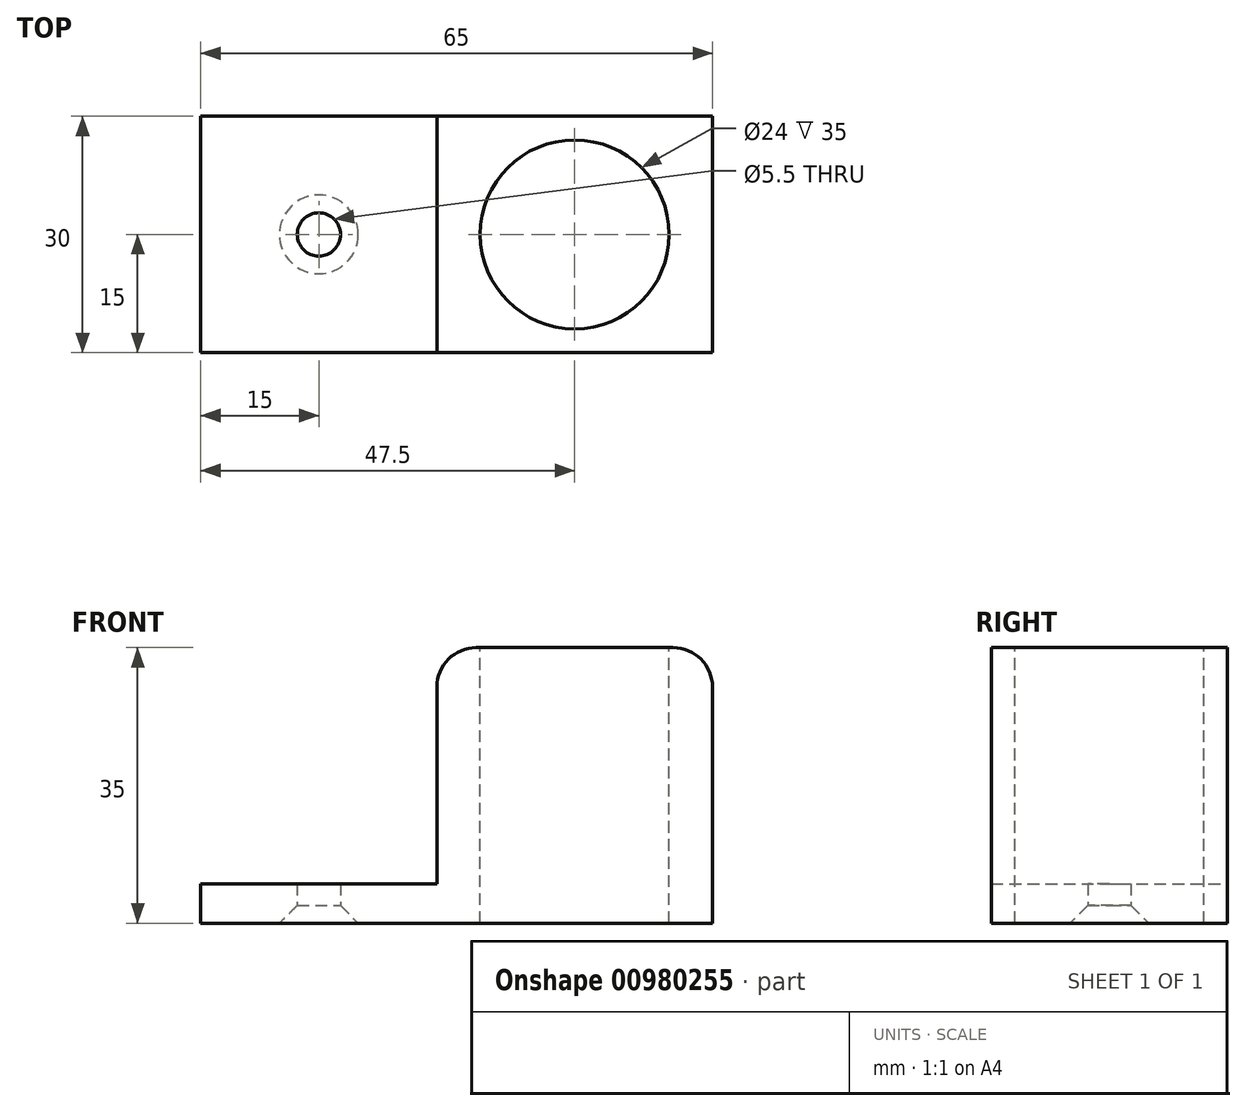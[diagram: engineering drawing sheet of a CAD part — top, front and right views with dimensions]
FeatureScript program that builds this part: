
annotation { "Feature Type Name" : "Feature", "Feature Type Description" : "" }
export const myFeature = defineFeature(function(context is Context, id is Id, definition is map)
    precondition{}
    {
        {
            var Q0;
            Q0=qCreatedBy(makeId("Front.planeOp"),FACE);
            var sketch = newSketch(context, id + "F0", { "sketchPlane" : qUnion([Q0])});
            skLineSegment(sketch, "E0", {"start": v(0, 0) * mm, "end": v(-65, 0) * mm});
            skLineSegment(sketch, "E1", {"start": v(-65, 0) * mm, "end": v(-65, 5) * mm});
            skLineSegment(sketch, "E2", {"start": v(-65, 5) * mm, "end": v(-35, 5) * mm});
            skLineSegment(sketch, "E3", {"start": v(-35, 5) * mm, "end": v(-35, 35) * mm});
            skLineSegment(sketch, "E4", {"start": v(-35, 35) * mm, "end": v(0, 35) * mm});
            skLineSegment(sketch, "E5", {"start": v(0, 35) * mm, "end": v(0, 0) * mm});
            skSolve(sketch);
        }
        {
            var Q0;
            Q0=makeQuery(id+"F0.imprint","IMPRINT",FACE,{"disambiguationData":[TD([[makeQuery(id+"F0.imprint","IMPRINT",EDGE,{"derivedFrom":sQuery(id+"F0.wireOp",EDGE,"E0")}),-1.0]])]});
            extrude(context, id + "F1", {"entities" : qUnion([Q0]), "depth" : 30 * mm, "offsetDistance" : 25 * mm});
        }
        {
            var Q0;
            Q0=makeQuery(id+"F1.opExtrude","SWEPT_FACE",FACE,{"disambiguationData":[OSD([sQuery(id+"F0.wireOp",EDGE,"E2")])]});
            var sketch = newSketch(context, id + "F2", { "sketchPlane" : qUnion([Q0])});
            skLineSegment(sketch, "E6", {"start": v(-35, 0) * mm, "end": v(-65, -30) * mm, "construction": true});
            skPoint(sketch, "E7", {"position": v(-50, -15) * mm});
            skSolve(sketch);
        }
        {
            var Q0;
            Q0=makeQuery(id+"F1.opExtrude","SWEPT_FACE",FACE,{"disambiguationData":[OSD([sQuery(id+"F0.wireOp",EDGE,"E4")])]});
            var sketch = newSketch(context, id + "F3", { "sketchPlane" : qUnion([Q0])});
            skLineSegment(sketch, "E8", {"start": v(0, 0) * mm, "end": v(-35, -30) * mm, "construction": true});
            skPoint(sketch, "E9", {"position": v(-17.5, -15) * mm});
            skCircle(sketch, "E10", {"center": v(-17.5, -15) * mm, "radius": 12 * mm});
            skSolve(sketch);
        }
        {
            var Q0;
            Q0=makeQuery(id+"F3.imprint","IMPRINT",FACE,{"disambiguationData":[TD([[makeQuery(id+"F3.imprint","IMPRINT",EDGE,{"derivedFrom":sQuery(id+"F3.wireOp",EDGE,"E10")}),1.0]])]});
            var Q1;
            Q1=makeQuery(id+"F1.opExtrude","SWEPT_FACE",FACE,{"disambiguationData":[OSD([sQuery(id+"F0.wireOp",EDGE,"E0")])]});
            extrude(context, id + "F4", {"entities" : qUnion([Q0]), "operationType" : NewBodyOperationType.REMOVE, "endBound" : BoundingType.UP_TO_SURFACE, "oppositeDirection" : true, "depth" : 25 * mm, "endBoundEntityFace" : qUnion([Q1]), "offsetDistance" : 25 * mm});
        }
        {
            var Q0;
            Q0=makeQuery(id+"F1.opExtrude","SWEPT_EDGE",EDGE,{"disambiguationData":[OSD([sQuery(id+"F0.wireOp",EDGE,"E4"),sQuery(id+"F0.wireOp",EDGE,"E5")])]});
            var Q1;
            Q1=makeQuery(id+"F1.opExtrude","SWEPT_EDGE",EDGE,{"disambiguationData":[OSD([sQuery(id+"F0.wireOp",EDGE,"E3"),sQuery(id+"F0.wireOp",EDGE,"E4")])]});
            fillet(context, id + "F5", {"entities" : qUnion([Q0, Q1]), "radius" : 5 * mm, "tangentPropagation" : true, "allowEdgeOverflow" : false});
        }
        {
            var Q0;
            Q0=makeQuery(id+"F1.opExtrude","SWEPT_FACE",FACE,{"disambiguationData":[OSD([sQuery(id+"F0.wireOp",EDGE,"E0")])]});
            var sketch = newSketch(context, id + "F6", { "sketchPlane" : qUnion([Q0])});
            skLineSegment(sketch, "E11.0", {"start": v(-35, 0) * mm, "end": v(-65, 30) * mm});
            skPoint(sketch, "E11.1", {"position": v(-50, 15) * mm});
            skSolve(sketch);
        }
        {
            var Q0;
            Q0=sQuery(id+"F6.wireOp",VERTEX,"E11.1");
            var Q1;
            Q1=makeQuery(id+"F1.opExtrude","SWEPT_BODY",BODY,{"disambiguationData":[OSD([sQuery(id+"F0.wireOp",EDGE,"E0"),sQuery(id+"F0.wireOp",EDGE,"E1"),sQuery(id+"F0.wireOp",EDGE,"E2"),sQuery(id+"F0.wireOp",EDGE,"E3"),sQuery(id+"F0.wireOp",EDGE,"E4"),sQuery(id+"F0.wireOp",EDGE,"E5")])]});
            hole(context, id + "F7", {"style" : HoleStyle.C_SINK, "endStyle" : HoleEndStyle.BLIND, "holeDiameter" : 5.5 * mm, "cSinkDiameter" : 10 * mm, "cSinkAngle" : 90 * degree, "majorDiameter" : 5 * mm, "holeDepth" : 16 * mm, "isTappedThrough" : true, "tappedDepth" : 12 * mm, "tapClearance" : 3, "locations" : qUnion([Q0]), "scope" : qUnion([Q1])});
        }
    });
